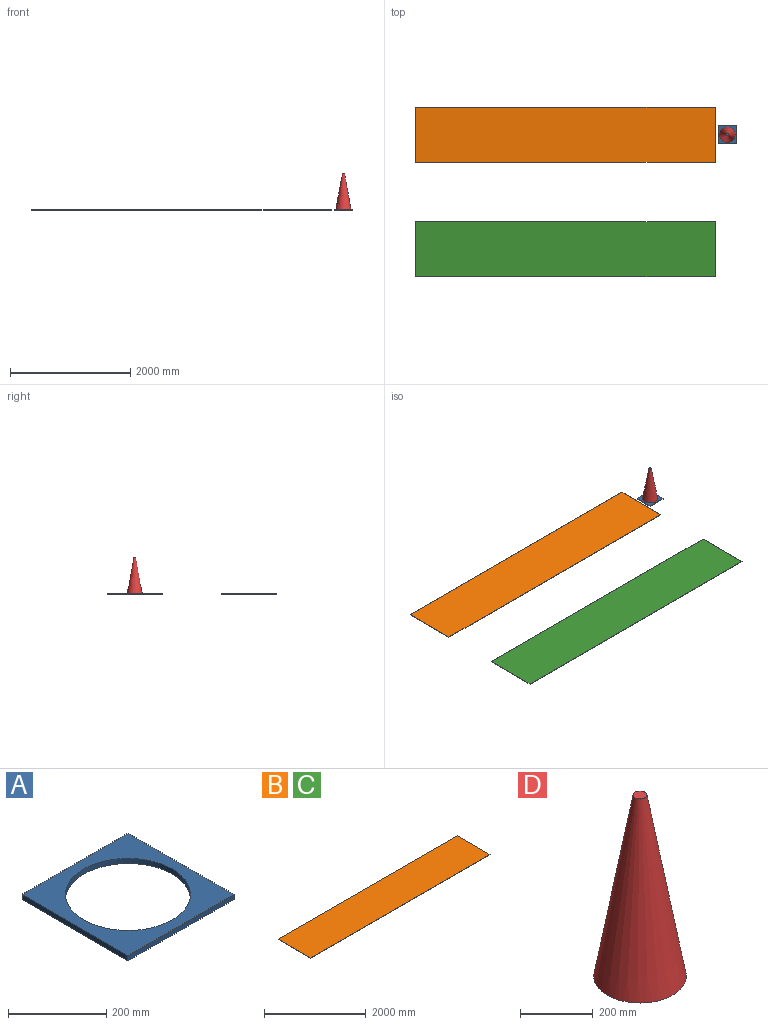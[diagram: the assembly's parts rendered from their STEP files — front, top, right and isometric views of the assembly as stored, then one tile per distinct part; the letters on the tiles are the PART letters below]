
ASSEMBLY  parts=4 mates=3
PART A: 7 faces, bbox 304.8x304.8x12.7 mm
  f0: plane 304.8x12.7mm, normal (0,1,0), area 3871mm2, adj f1,f4,f5,f6
  f1: plane 304.8x12.7mm, normal (-1,0,0), area 3871mm2, adj f0,f2,f5,f6
  f2: plane 304.8x12.7mm, normal (0,-1,0), area 3871mm2, adj f1,f4,f5,f6
  f3: cylinder r=127mm len=254mm, axis (0,0,1), area 10134.1mm2, adj f5,f6
  f4: plane 304.8x12.7mm, normal (1,0,0), area 3871mm2, adj f0,f2,f5,f6
  f5: plane 304.8x304.8mm, normal (0,0,-1), area 42232.3mm2, adj f0,f1,f2,f3,f4
  f6: plane 304.8x304.8mm, normal (0,0,1), area 42232.3mm2, adj f0,f1,f2,f3,f4
PART B: 6 faces, bbox 4978.4x914.4x6.4 mm
  f0: plane 914.4x6.35mm, normal (1,0,0), area 5806.4mm2, adj f1,f3,f4,f5
  f1: plane 4978.4x6.35mm, normal (0,1,0), area 31612.8mm2, adj f0,f2,f4,f5
  f2: plane 914.4x6.35mm, normal (-1,0,0), area 5806.4mm2, adj f1,f3,f4,f5
  f3: plane 4978.4x6.35mm, normal (0,-1,0), area 31612.8mm2, adj f0,f2,f4,f5
  f4: plane 4978.4x914.4mm, normal (0,0,1), area 4552249mm2, adj f0,f1,f2,f3
  f5: plane 4978.4x914.4mm, normal (0,0,-1), area 4552249mm2, adj f0,f1,f2,f3
PART C: same geometry as B
PART D: 3 faces, bbox 254x254x609.6 mm
  f0: plane 254x254mm, normal (0,0,-1), area 50670.7mm2, adj f2
  f1: plane 38.1x38.1mm, normal (0,0,1), area 1140.1mm2, adj f2
  f2: cone r=127mm half-angle=10deg, axis (0,0,-1), area 284054.2mm2, adj f0,f1
PLACE A t=(3588.16,1841.98,-1004.62)mm
PLACE B t=(895.76,1841.98,-1010.97)mm
PLACE C t=(895.76,-63.02,-1010.97)mm fixed
PLACE D t=(3588.16,1841.98,-1004.62)mm
MATE planar B.f4 <-> C.f4  axis (0,0,1) through (895.76,1841.98,-1004.62)mm
MATE cylindrical A.f3 <-> D.f2  axis (0,0,1) through (3588.16,1841.98,-1004.62)mm
MATE planar A.f6 <-> B.f4  axis (0,0,1) through (3435.76,1841.98,-1004.62)mm
